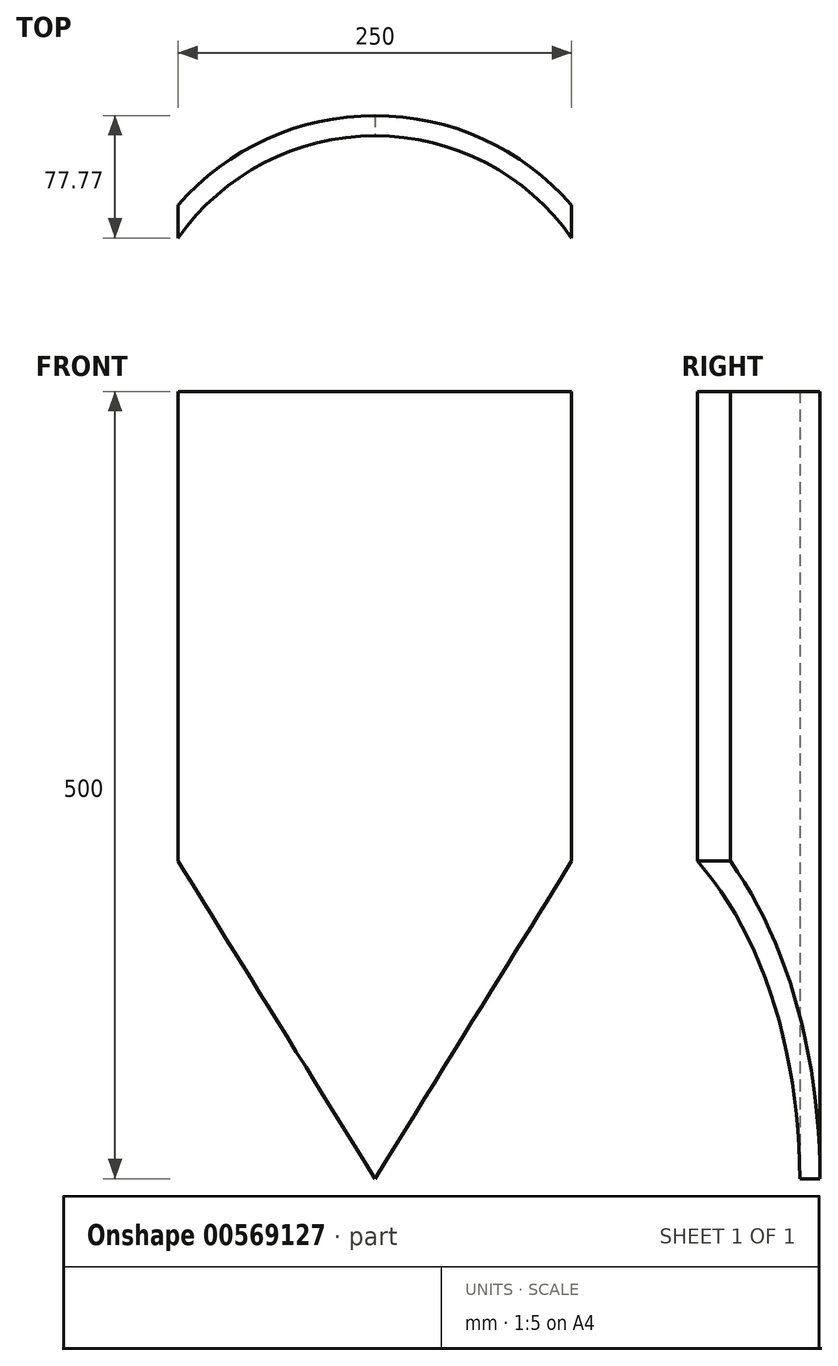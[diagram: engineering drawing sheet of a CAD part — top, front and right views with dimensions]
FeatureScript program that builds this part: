
annotation { "Feature Type Name" : "Feature", "Feature Type Description" : "" }
export const myFeature = defineFeature(function(context is Context, id is Id, definition is map)
    precondition{}
    {
        {
            var Q0;
            Q0=qCreatedBy(makeId("Top.planeOp"),FACE);
            var sketch = newSketch(context, id + "F0", { "sketchPlane" : qUnion([Q0])});
            skArc(sketch, "E0", {"start": v(125, 108.7) * mm, "mid": v(0, 165.65) * mm, "end": v(-125, 108.7) * mm});
            skLineSegment(sketch, "E1", {"start": v(-125, 108.7) * mm, "end": v(-125, 87.88) * mm});
            skLineSegment(sketch, "E2", {"start": v(125, 87.88) * mm, "end": v(125, 108.7) * mm});
            skArc(sketch, "E3", {"start": v(125, 87.88) * mm, "mid": v(0, 152.8) * mm, "end": v(-125, 87.88) * mm});
            skSolve(sketch);
        }
        {
            var Q0;
            Q0=makeQuery(id+"F0.imprint","IMPRINT",FACE,{"disambiguationData":[TD([[makeQuery(id+"F0.imprint","IMPRINT",EDGE,{"derivedFrom":sQuery(id+"F0.wireOp",EDGE,"E0")}),1.0]])]});
            extrude(context, id + "F1", {"entities" : qUnion([Q0]), "depth" : 250 * mm, "offsetDistance" : 25 * mm, "hasSecondDirection" : true, "secondDirectionOppositeDirection" : true, "secondDirectionDepth" : 250 * mm});
        }
        {
            var Q0;
            Q0=qCreatedBy(makeId("Front.planeOp"),FACE);
            var sketch = newSketch(context, id + "F2", { "sketchPlane" : qUnion([Q0])});
            skLineSegment(sketch, "E4", {"start": v(125, -48.3) * mm, "end": v(0, -250) * mm});
            skLineSegment(sketch, "E5", {"start": v(0, -250) * mm, "end": v(-125, -48.3) * mm});
            skLineSegment(sketch, "E6", {"start": v(-125, -48.3) * mm, "end": v(-125, -250.16) * mm});
            skLineSegment(sketch, "E7", {"start": v(-125, -250.16) * mm, "end": v(0, -250) * mm});
            skLineSegment(sketch, "E8", {"start": v(125, -48.3) * mm, "end": v(125, -250) * mm});
            skLineSegment(sketch, "E9", {"start": v(125, -250) * mm, "end": v(0, -250) * mm});
            skSolve(sketch);
        }
        {
            var Q0;
            Q0=makeQuery(id+"F2.imprint","IMPRINT",FACE,{"disambiguationData":[TD([[makeQuery(id+"F2.imprint","IMPRINT",EDGE,{"derivedFrom":sQuery(id+"F2.wireOp",EDGE,"E5")}),1.0]])]});
            var Q1;
            Q1=makeQuery(id+"F2.imprint","IMPRINT",FACE,{"disambiguationData":[TD([[makeQuery(id+"F2.imprint","IMPRINT",EDGE,{"derivedFrom":sQuery(id+"F2.wireOp",EDGE,"E4")}),1.0]])]});
            extrude(context, id + "F3", {"entities" : qUnion([Q0, Q1]), "operationType" : NewBodyOperationType.REMOVE, "endBound" : BoundingType.THROUGH_ALL, "oppositeDirection" : true, "depth" : 100000 * mm, "offsetDistance" : 25 * mm});
        }
    });
